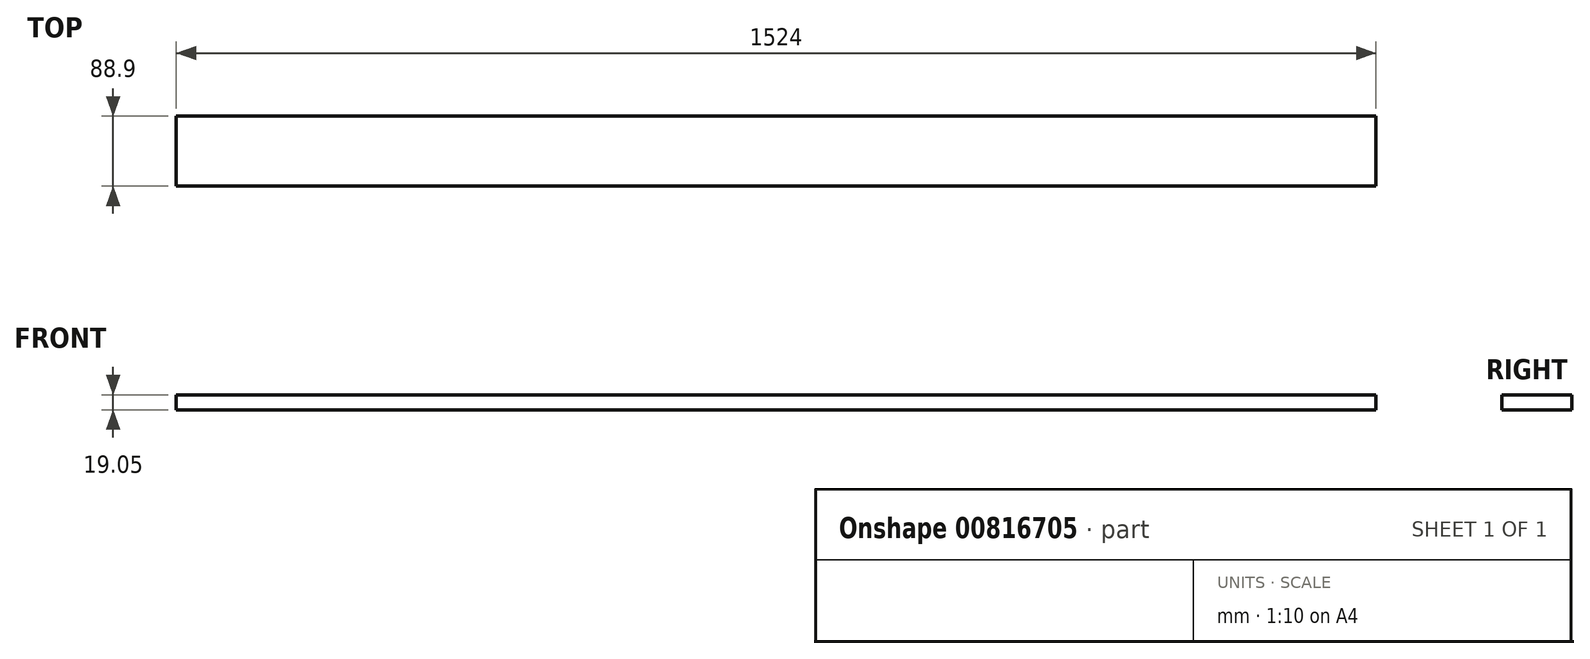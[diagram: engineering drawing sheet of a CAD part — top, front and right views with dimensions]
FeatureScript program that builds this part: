
annotation { "Feature Type Name" : "Feature", "Feature Type Description" : "" }
export const myFeature = defineFeature(function(context is Context, id is Id, definition is map)
    precondition{}
    {
        {
            var Q0;
            Q0=qCreatedBy(makeId("Top.planeOp"),FACE);
            var sketch = newSketch(context, id + "F0", { "sketchPlane" : qUnion([Q0])});
            skLineSegment(sketch, "E0.bottom", {"start": v(0, 0) * mm, "end": v(1524, 0) * mm});
            skLineSegment(sketch, "E0.top", {"start": v(0, 88.9) * mm, "end": v(1524, 88.9) * mm});
            skLineSegment(sketch, "E0.left", {"start": v(0, 0) * mm, "end": v(0, 88.9) * mm});
            skLineSegment(sketch, "E0.right", {"start": v(1524, 0) * mm, "end": v(1524, 88.9) * mm});
            skSolve(sketch);
        }
        {
            var Q0;
            Q0 = qSketchRegion(id + "F0", true);
            extrude(context, id + "F1", {"entities" : qUnion([Q0]), "depth" : 19.05 * mm, "offsetDistance" : 25.4 * mm});
        }
    });
